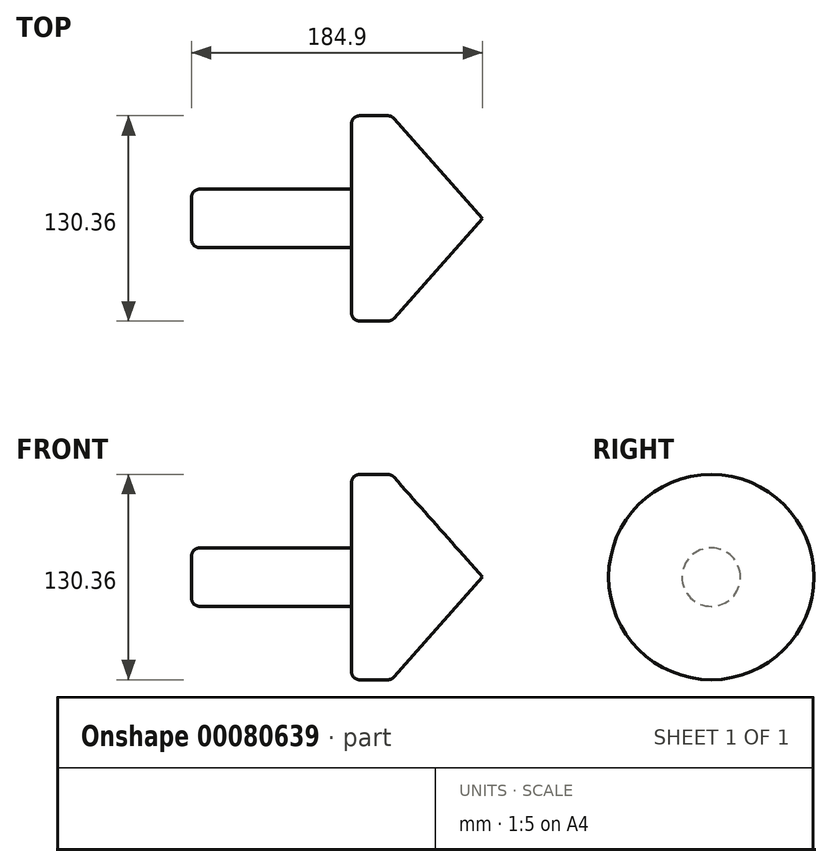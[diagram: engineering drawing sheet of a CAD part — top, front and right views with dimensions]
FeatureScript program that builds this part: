
annotation { "Feature Type Name" : "Feature", "Feature Type Description" : "" }
export const myFeature = defineFeature(function(context is Context, id is Id, definition is map)
    precondition{}
    {
        {
            var Q0;
            Q0=qCreatedBy(makeId("Front.planeOp"),FACE);
            var sketch = newSketch(context, id + "F0", { "sketchPlane" : qUnion([Q0])});
            skLineSegment(sketch, "E0", {"start": v(0, 0) * mm, "end": v(57.9, 0) * mm});
            skLineSegment(sketch, "E1", {"start": v(57.9, 0) * mm, "end": v(0, 65.18) * mm});
            skLineSegment(sketch, "E2", {"start": v(0, 65.18) * mm, "end": v(0, 0) * mm});
            skSolve(sketch);
        }
        {
            var Q0;
            Q0=makeQuery(id+"F0.imprint","IMPRINT",FACE,{"disambiguationData":[TD([[makeQuery(id+"F0.imprint","IMPRINT",EDGE,{"derivedFrom":sQuery(id+"F0.wireOp",EDGE,"E0")}),1.0]])]});
            var Q1;
            Q1=sQuery(id+"F0.wireOp",EDGE,"E0");
            revolve(context, id + "F1", {"entities" : qUnion([Q0]), "axis" : qUnion([Q1]), "revolveType" : RevolveType.FULL});
        }
        {
            var Q0;
            Q0=makeQuery(id+"F1.opRevolve","SWEPT_FACE",FACE,{"disambiguationData":[OSD([sQuery(id+"F0.wireOp",EDGE,"E2")])]});
            extrude(context, id + "F2", {"entities" : qUnion([Q0]), "operationType" : NewBodyOperationType.ADD, "depth" : 25.4 * mm});
        }
        {
            var Q0;
            Q0=makeQuery(id+"F2.opExtrude","CAP_FACE",FACE,{"disambiguationData":[OSD([sQuery(id+"F0.wireOp",EDGE,"E2")])],"isStart":false});
            var sketch = newSketch(context, id + "F3", { "sketchPlane" : qUnion([Q0])});
            skCircle(sketch, "E3", {"center": v(0, 0) * mm, "radius": 18.55 * mm});
            skSolve(sketch);
        }
        {
            var Q0;
            Q0=makeQuery(id+"F3.imprint","IMPRINT",FACE,{"disambiguationData":[TD([[makeQuery(id+"F3.imprint","IMPRINT",EDGE,{"derivedFrom":sQuery(id+"F3.wireOp",EDGE,"E3")}),1.0]])]});
            extrude(context, id + "F4", {"entities" : qUnion([Q0]), "operationType" : NewBodyOperationType.ADD, "depth" : 101.6 * mm});
        }
        {
            var Q0;
            {var subQ0=sQuery(id+"F0.wireOp",EDGE,"E2");var subQ1=sQuery(id+"F0.wireOp",EDGE,"E1");Q0=makeQuery(id+"F2.boolean.opBoolean","MERGE",EDGE,{"derivedFrom":[makeQuery(id+"F1.opRevolve","SWEPT_EDGE",EDGE,{"disambiguationData":[OSD([subQ1,subQ0])]}),makeQuery(id+"F2.opExtrude","CAP_EDGE",EDGE,{"disambiguationData":[OSD([subQ1,subQ0])],"isStart":true})]});}
            fillet(context, id + "F5", {"entities" : qUnion([Q0]), "radius" : 5.08 * mm, "tangentPropagation" : true, "allowEdgeOverflow" : false});
        }
        {
            var Q0;
            Q0=makeQuery(id+"F2.opExtrude","CAP_EDGE",EDGE,{"disambiguationData":[OSD([sQuery(id+"F0.wireOp",EDGE,"E1"),sQuery(id+"F0.wireOp",EDGE,"E2")])],"isStart":false});
            fillet(context, id + "F6", {"entities" : qUnion([Q0]), "radius" : 5.08 * mm, "tangentPropagation" : true, "allowEdgeOverflow" : false});
        }
        {
            var Q0;
            Q0=makeQuery(id+"F4.opExtrude","CAP_EDGE",EDGE,{"disambiguationData":[OSD([sQuery(id+"F3.wireOp",EDGE,"E3")])],"isStart":false});
            fillet(context, id + "F7", {"entities" : qUnion([Q0]), "radius" : 5.08 * mm, "tangentPropagation" : true, "allowEdgeOverflow" : false});
        }
    });
